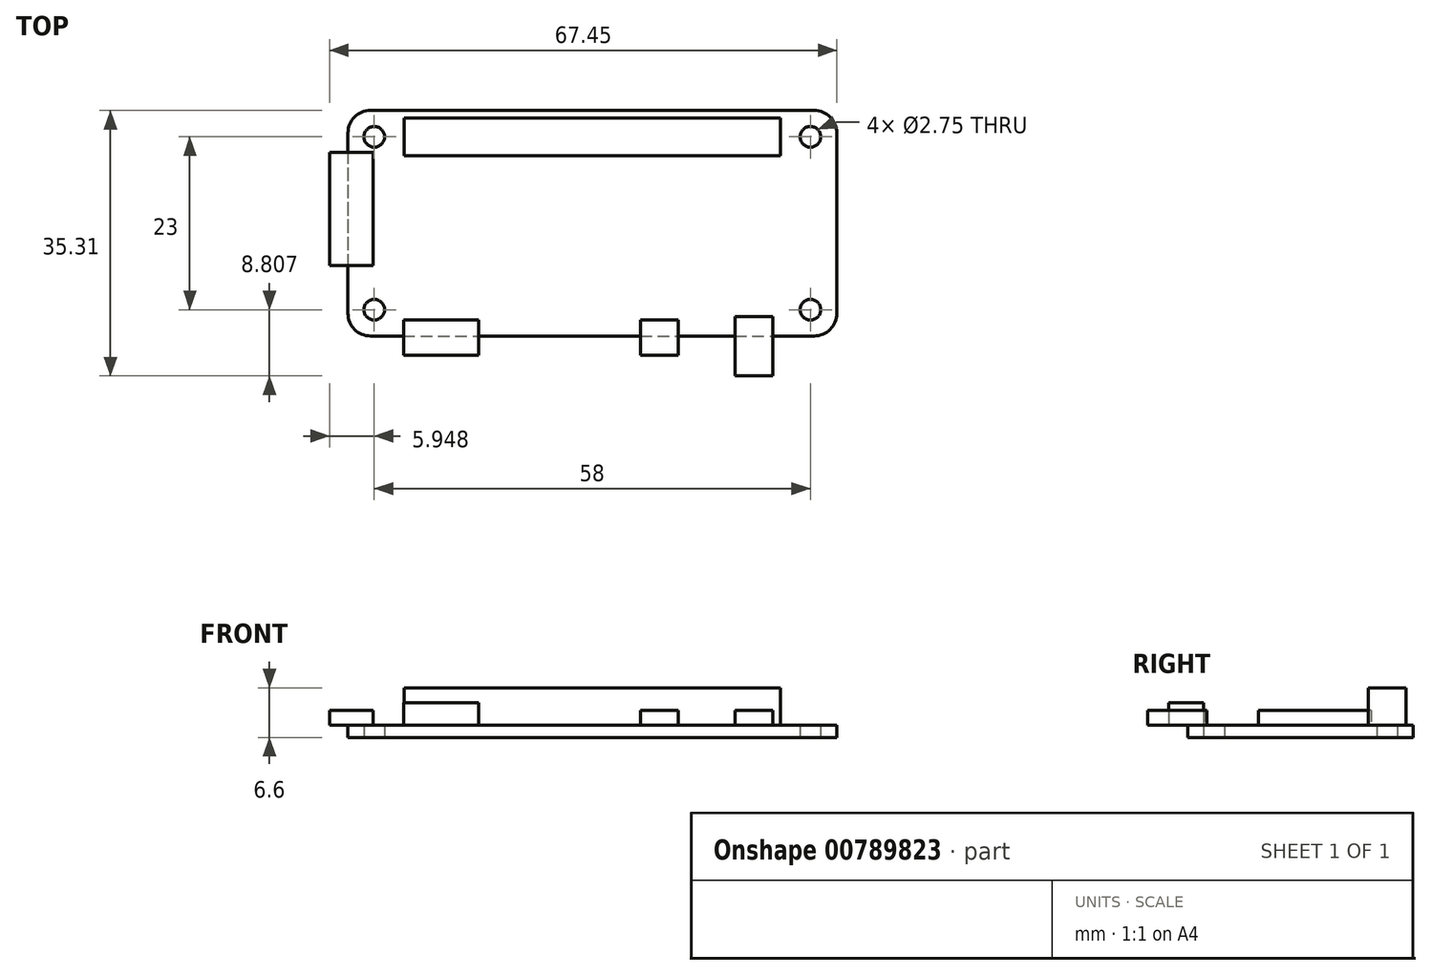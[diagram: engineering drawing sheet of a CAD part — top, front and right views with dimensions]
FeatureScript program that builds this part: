
annotation { "Feature Type Name" : "Feature", "Feature Type Description" : "" }
export const myFeature = defineFeature(function(context is Context, id is Id, definition is map)
    precondition{}
    {
        {
            var Q0;
            Q0=qCreatedBy(makeId("Top.planeOp"),FACE);
            var sketch = newSketch(context, id + "F0", { "sketchPlane" : qUnion([Q0])});
            skLineSegment(sketch, "E0", {"start": v(-85.3, -108.5) * mm, "end": v(-43.8, -108.5) * mm, "construction": true});
            skLineSegment(sketch, "E1", {"start": v(-63.03, -117.27) * mm, "end": v(-63.03, -97.18) * mm, "construction": true});
            skLineSegment(sketch, "E2.bottom", {"start": v(-92.53, -93.5) * mm, "end": v(-33.53, -93.5) * mm});
            skLineSegment(sketch, "E2.top", {"start": v(-92.53, -123.5) * mm, "end": v(-33.53, -123.5) * mm});
            skLineSegment(sketch, "E2.left", {"start": v(-95.53, -96.5) * mm, "end": v(-95.53, -120.5) * mm});
            skLineSegment(sketch, "E2.right", {"start": v(-30.53, -96.5) * mm, "end": v(-30.53, -120.5) * mm});
            skPoint(sketch, "E3.visualSharp", {"position": v(-95.53, -93.5) * mm});
            skArc(sketch, "E3.filletArc", {"start": v(-92.53, -93.5) * mm, "mid": v(-94.65, -94.37) * mm, "end": v(-95.53, -96.5) * mm});
            skPoint(sketch, "E4.visualSharp", {"position": v(-30.53, -93.5) * mm});
            skArc(sketch, "E4.filletArc", {"start": v(-30.53, -96.5) * mm, "mid": v(-31.41, -94.37) * mm, "end": v(-33.53, -93.5) * mm});
            skPoint(sketch, "E5.visualSharp", {"position": v(-30.53, -123.5) * mm});
            skArc(sketch, "E5.filletArc", {"start": v(-33.53, -123.5) * mm, "mid": v(-31.41, -122.61) * mm, "end": v(-30.53, -120.5) * mm});
            skPoint(sketch, "E6.visualSharp", {"position": v(-95.53, -123.5) * mm});
            skArc(sketch, "E6.filletArc", {"start": v(-95.53, -120.5) * mm, "mid": v(-94.65, -122.61) * mm, "end": v(-92.53, -123.5) * mm});
            skCircle(sketch, "E7", {"center": v(-34.03, -97) * mm, "radius": 1.38 * mm});
            skCircle(sketch, "E8.MirrorC", {"center": v(-92.03, -97) * mm, "radius": 1.38 * mm});
            skCircle(sketch, "E9.MirrorC", {"center": v(-34.03, -120) * mm, "radius": 1.38 * mm});
            skCircle(sketch, "E10.MirrorC", {"center": v(-92.03, -120) * mm, "radius": 1.38 * mm});
            skSolve(sketch);
        }
        {
            var Q0;
            Q0=makeQuery(id+"F0.imprint","IMPRINT",FACE,{"disambiguationData":[TD([[makeQuery(id+"F0.imprint","IMPRINT",EDGE,{"derivedFrom":sQuery(id+"F0.wireOp",EDGE,"E2.bottom")}),-1.0]])]});
            extrude(context, id + "F1", {"entities" : qUnion([Q0]), "depth" : 1.6 * mm, "offsetDistance" : 25 * mm});
        }
        {
            var Q0;
            Q0=makeQuery(id+"F1.opExtrude","CAP_FACE",FACE,{"disambiguationData":[OSD([sQuery(id+"F0.wireOp",EDGE,"E2.bottom"),sQuery(id+"F0.wireOp",EDGE,"E2.top"),sQuery(id+"F0.wireOp",EDGE,"E2.left"),sQuery(id+"F0.wireOp",EDGE,"E2.right"),sQuery(id+"F0.wireOp",EDGE,"E3.filletArc"),sQuery(id+"F0.wireOp",EDGE,"E4.filletArc"),sQuery(id+"F0.wireOp",EDGE,"E5.filletArc"),sQuery(id+"F0.wireOp",EDGE,"E6.filletArc"),sQuery(id+"F0.wireOp",EDGE,"E7"),sQuery(id+"F0.wireOp",EDGE,"E8.MirrorC"),sQuery(id+"F0.wireOp",EDGE,"E9.MirrorC"),sQuery(id+"F0.wireOp",EDGE,"E10.MirrorC")])],"isStart":false});
            var sketch = newSketch(context, id + "F2", { "sketchPlane" : qUnion([Q0])});
            skLineSegment(sketch, "E11.bottom", {"start": v(-88.13, -121.37) * mm, "end": v(-78.13, -121.37) * mm});
            skLineSegment(sketch, "E11.top", {"start": v(-88.13, -126.04) * mm, "end": v(-78.13, -126.04) * mm});
            skLineSegment(sketch, "E11.left", {"start": v(-78.13, -121.37) * mm, "end": v(-78.13, -126.04) * mm});
            skLineSegment(sketch, "E11.right", {"start": v(-88.13, -121.37) * mm, "end": v(-88.13, -126.04) * mm});
            skLineSegment(sketch, "E12.bottom", {"start": v(-56.63, -121.33) * mm, "end": v(-51.63, -121.33) * mm});
            skLineSegment(sketch, "E12.top", {"start": v(-56.63, -126.04) * mm, "end": v(-51.63, -126.04) * mm});
            skLineSegment(sketch, "E12.left", {"start": v(-56.63, -121.33) * mm, "end": v(-56.63, -126.04) * mm});
            skLineSegment(sketch, "E12.right", {"start": v(-51.63, -121.33) * mm, "end": v(-51.63, -126.04) * mm});
            skLineSegment(sketch, "E13.bottom", {"start": v(-44.03, -128.8) * mm, "end": v(-39.03, -128.8) * mm});
            skLineSegment(sketch, "E13.top", {"start": v(-44.03, -120.94) * mm, "end": v(-39.03, -120.94) * mm});
            skLineSegment(sketch, "E13.left", {"start": v(-44.03, -128.8) * mm, "end": v(-44.03, -120.94) * mm});
            skLineSegment(sketch, "E13.right", {"start": v(-39.03, -128.8) * mm, "end": v(-39.03, -120.94) * mm});
            skLineSegment(sketch, "E14.bottom", {"start": v(-97.98, -99.1) * mm, "end": v(-92.2, -99.1) * mm});
            skLineSegment(sketch, "E14.top", {"start": v(-97.98, -114.1) * mm, "end": v(-92.2, -114.1) * mm});
            skLineSegment(sketch, "E14.left", {"start": v(-97.98, -99.1) * mm, "end": v(-97.98, -114.1) * mm});
            skLineSegment(sketch, "E14.right", {"start": v(-92.2, -99.1) * mm, "end": v(-92.2, -114.1) * mm});
            skLineSegment(sketch, "E15.bottom", {"start": v(-88.03, -99.5) * mm, "end": v(-38.03, -99.5) * mm});
            skLineSegment(sketch, "E15.top", {"start": v(-88.03, -94.5) * mm, "end": v(-38.03, -94.5) * mm});
            skLineSegment(sketch, "E15.left", {"start": v(-88.03, -99.5) * mm, "end": v(-88.03, -94.5) * mm});
            skLineSegment(sketch, "E15.right", {"start": v(-38.03, -99.5) * mm, "end": v(-38.03, -94.5) * mm});
            skLineSegment(sketch, "E16", {"start": v(-83.13, -134.5) * mm, "end": v(-83.13, -122.62) * mm, "construction": true});
            skLineSegment(sketch, "E17", {"start": v(-54.13, -134.15) * mm, "end": v(-54.13, -122.1) * mm, "construction": true});
            skLineSegment(sketch, "E18", {"start": v(-41.53, -134.33) * mm, "end": v(-41.53, -125.2) * mm, "construction": true});
            skLineSegment(sketch, "E19", {"start": v(-97.17, -106.6) * mm, "end": v(-90.55, -106.6) * mm, "construction": true});
            skLineSegment(sketch, "E20", {"start": v(-63.03, -81.45) * mm, "end": v(-63.03, -103.15) * mm, "construction": true});
            skPoint(sketch, "E21", {"position": v(-92.03, -97) * mm});
            skLineSegment(sketch, "E22", {"start": v(-81.35, -97) * mm, "end": v(-46.94, -97) * mm, "construction": true});
            skPoint(sketch, "E23", {"position": v(-88.03, -97) * mm});
            skSolve(sketch);
        }
        {
            var Q0;
            {var subQ0=sQuery(id+"F2.wireOp",EDGE,"E14.left");Q0=makeQuery(id+"F2.imprint","IMPRINT",FACE,{"disambiguationData":[TD([[makeQuery(id+"F2.imprint","IMPRINT",EDGE,{"derivedFrom":subQ0}),1.0]])]});}
            var Q1;
            {var subQ0=sQuery(id+"F2.wireOp",EDGE,"E14.right");Q1=makeQuery(id+"F2.imprint","IMPRINT",FACE,{"disambiguationData":[TD([[makeQuery(id+"F2.imprint","IMPRINT",EDGE,{"derivedFrom":subQ0}),-1.0]])]});}
            extrude(context, id + "F3", {"entities" : qUnion([Q0, Q1]), "operationType" : NewBodyOperationType.ADD, "depth" : 2 * mm, "offsetDistance" : 25 * mm});
        }
        {
            var Q0;
            Q0=makeQuery(id+"F2.imprint","IMPRINT",FACE,{"disambiguationData":[TD([[makeQuery(id+"F2.imprint","IMPRINT",EDGE,{"derivedFrom":sQuery(id+"F2.wireOp",EDGE,"E15.bottom")}),1.0]])]});
            extrude(context, id + "F4", {"entities" : qUnion([Q0]), "operationType" : NewBodyOperationType.ADD, "depth" : 5 * mm, "offsetDistance" : 25 * mm});
        }
        {
            var Q0;
            {var subQ0=sQuery(id+"F2.wireOp",EDGE,"E12.top");Q0=makeQuery(id+"F2.imprint","IMPRINT",FACE,{"disambiguationData":[TD([[makeQuery(id+"F2.imprint","IMPRINT",EDGE,{"derivedFrom":subQ0}),1.0]])]});}
            var Q1;
            {var subQ0=sQuery(id+"F2.wireOp",EDGE,"E12.bottom");Q1=makeQuery(id+"F2.imprint","IMPRINT",FACE,{"disambiguationData":[TD([[makeQuery(id+"F2.imprint","IMPRINT",EDGE,{"derivedFrom":subQ0}),-1.0]])]});}
            var Q2;
            {var subQ0=sQuery(id+"F2.wireOp",EDGE,"E13.top");Q2=makeQuery(id+"F2.imprint","IMPRINT",FACE,{"disambiguationData":[TD([[makeQuery(id+"F2.imprint","IMPRINT",EDGE,{"derivedFrom":subQ0}),-1.0]])]});}
            var Q3;
            {var subQ0=sQuery(id+"F2.wireOp",EDGE,"E13.bottom");Q3=makeQuery(id+"F2.imprint","IMPRINT",FACE,{"disambiguationData":[TD([[makeQuery(id+"F2.imprint","IMPRINT",EDGE,{"derivedFrom":subQ0}),1.0]])]});}
            extrude(context, id + "F5", {"entities" : qUnion([Q0, Q1, Q2, Q3]), "operationType" : NewBodyOperationType.ADD, "depth" : 2 * mm, "offsetDistance" : 25 * mm});
        }
        {
            var Q0;
            {var subQ0=sQuery(id+"F2.wireOp",EDGE,"E11.bottom");Q0=makeQuery(id+"F2.imprint","IMPRINT",FACE,{"disambiguationData":[TD([[makeQuery(id+"F2.imprint","IMPRINT",EDGE,{"derivedFrom":subQ0}),-1.0]])]});}
            var Q1;
            {var subQ0=sQuery(id+"F2.wireOp",EDGE,"E11.top");Q1=makeQuery(id+"F2.imprint","IMPRINT",FACE,{"disambiguationData":[TD([[makeQuery(id+"F2.imprint","IMPRINT",EDGE,{"derivedFrom":subQ0}),1.0]])]});}
            extrude(context, id + "F6", {"entities" : qUnion([Q0, Q1]), "operationType" : NewBodyOperationType.ADD, "depth" : 3 * mm, "offsetDistance" : 25 * mm});
        }
    });
